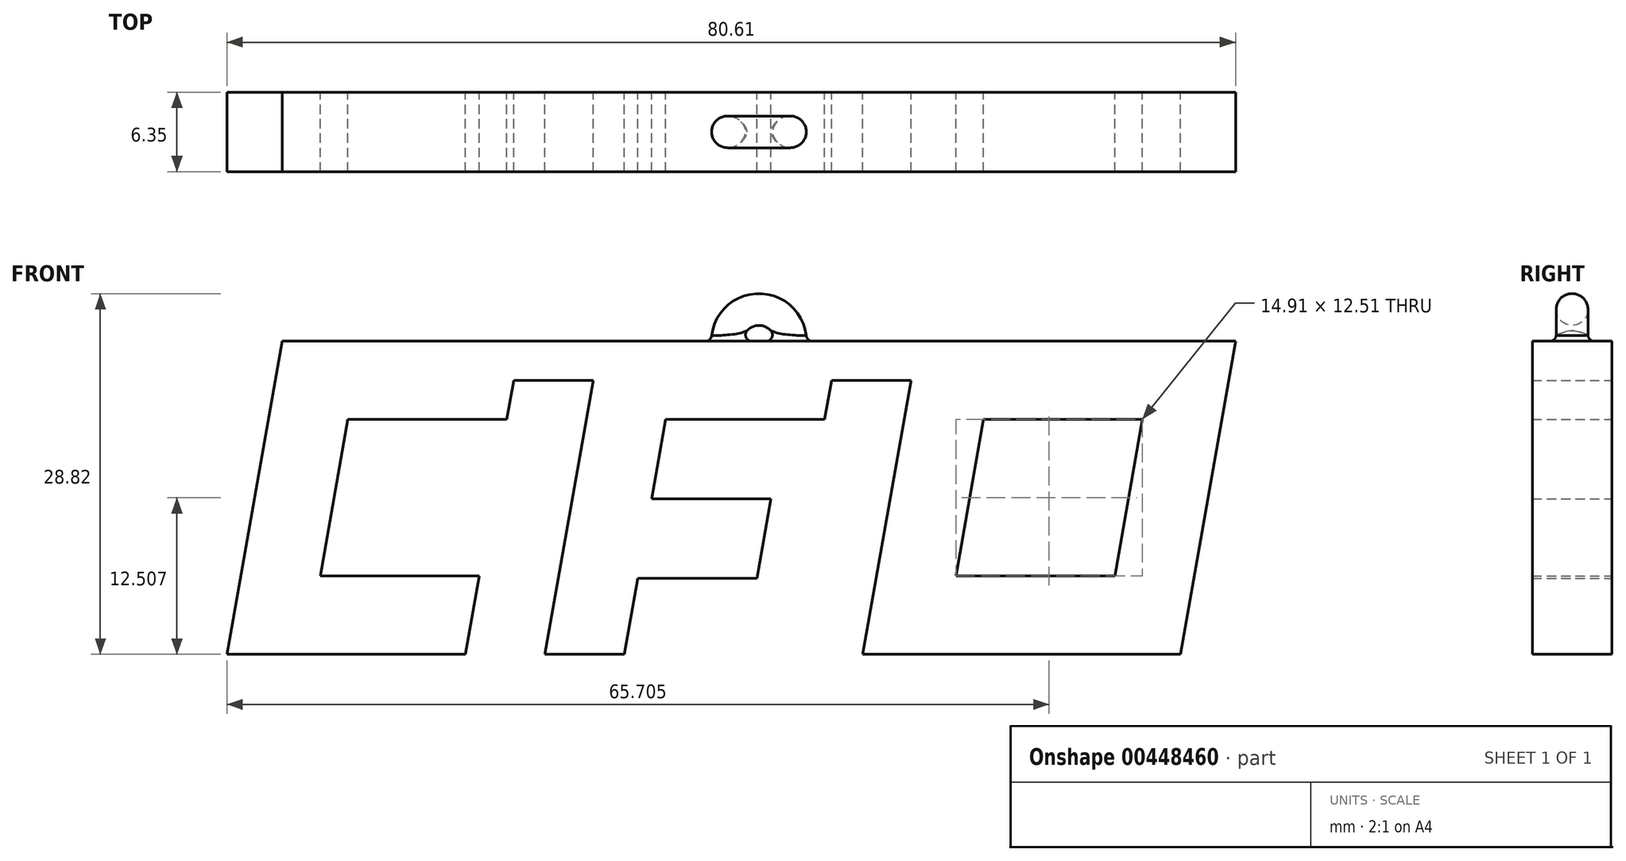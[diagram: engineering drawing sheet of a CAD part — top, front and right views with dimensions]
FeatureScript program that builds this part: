
annotation { "Feature Type Name" : "Feature", "Feature Type Description" : "" }
export const myFeature = defineFeature(function(context is Context, id is Id, definition is map)
    precondition{}
    {
        {
            var Q0;
            Q0=qCreatedBy(makeId("Front.planeOp"),FACE);
            var sketch = newSketch(context, id + "F0", { "sketchPlane" : qUnion([Q0])});
            skLineSegment(sketch, "E0", {"start": v(0, 0) * mm, "end": v(4.41, 25.01) * mm});
            skLineSegment(sketch, "E1", {"start": v(0, 0) * mm, "end": v(25.4, 0) * mm});
            skLineSegment(sketch, "E2", {"start": v(4.41, 25.01) * mm, "end": v(29.81, 25.01) * mm});
            skLineSegment(sketch, "E3", {"start": v(0, 0) * mm, "end": v(0, 25.4) * mm});
            skLineSegment(sketch, "E4", {"start": v(29.81, 25.01) * mm, "end": v(28.7, 18.76) * mm});
            skLineSegment(sketch, "E5", {"start": v(25.4, 0) * mm, "end": v(26.5, 6.25) * mm});
            skLineSegment(sketch, "E6", {"start": v(26.5, 6.25) * mm, "end": v(7.45, 6.25) * mm});
            skLineSegment(sketch, "E7", {"start": v(28.7, 18.76) * mm, "end": v(9.66, 18.76) * mm});
            skLineSegment(sketch, "E8", {"start": v(9.66, 18.76) * mm, "end": v(7.45, 6.25) * mm});
            skLineSegment(sketch, "E9", {"start": v(25.4, 0) * mm, "end": v(29.81, 25.01) * mm});
            skLineSegment(sketch, "E10", {"start": v(29.81, 25.01) * mm, "end": v(55.21, 25.01) * mm});
            skLineSegment(sketch, "E11", {"start": v(55.21, 25.01) * mm, "end": v(54.1, 18.76) * mm});
            skLineSegment(sketch, "E12", {"start": v(25.4, 0) * mm, "end": v(31.75, 0) * mm});
            skLineSegment(sketch, "E13", {"start": v(31.75, 0) * mm, "end": v(36.16, 25.01) * mm});
            skLineSegment(sketch, "E14", {"start": v(54.1, 18.76) * mm, "end": v(35.06, 18.76) * mm});
            skLineSegment(sketch, "E15", {"start": v(33.94, 12.41) * mm, "end": v(52.99, 12.41) * mm});
            skLineSegment(sketch, "E16", {"start": v(54.1, 18.76) * mm, "end": v(48.73, -11.73) * mm});
            skLineSegment(sketch, "E17", {"start": v(32.82, 6.06) * mm, "end": v(51.87, 6.06) * mm});
            skLineSegment(sketch, "E18", {"start": v(43.46, 12.41) * mm, "end": v(42.34, 6.06) * mm});
            skLineSegment(sketch, "E19", {"start": v(50.8, 0) * mm, "end": v(76.2, 0) * mm});
            skLineSegment(sketch, "E20", {"start": v(76.2, 0) * mm, "end": v(80.61, 25.01) * mm});
            skLineSegment(sketch, "E21", {"start": v(80.61, 25.01) * mm, "end": v(74.26, 25.01) * mm});
            skLineSegment(sketch, "E22", {"start": v(74.26, 25.01) * mm, "end": v(69.85, 0) * mm});
            skLineSegment(sketch, "E23", {"start": v(55.21, 25.01) * mm, "end": v(61.56, 25.01) * mm});
            skLineSegment(sketch, "E24", {"start": v(61.56, 25.01) * mm, "end": v(57.15, 0) * mm});
            skLineSegment(sketch, "E25", {"start": v(61.56, 25.01) * mm, "end": v(74.26, 25.01) * mm});
            skLineSegment(sketch, "E26", {"start": v(67.91, 25.01) * mm, "end": v(66.8, 18.76) * mm});
            skLineSegment(sketch, "E27", {"start": v(66.8, 18.76) * mm, "end": v(60.46, 18.76) * mm});
            skLineSegment(sketch, "E28", {"start": v(60.46, 18.76) * mm, "end": v(73.16, 18.76) * mm});
            skLineSegment(sketch, "E29", {"start": v(63.5, 0) * mm, "end": v(64.6, 6.25) * mm});
            skLineSegment(sketch, "E30", {"start": v(64.6, 6.25) * mm, "end": v(58.25, 6.25) * mm});
            skLineSegment(sketch, "E31", {"start": v(58.25, 6.25) * mm, "end": v(70.95, 6.25) * mm});
            skLineSegment(sketch, "E32", {"start": v(23.46, 25.01) * mm, "end": v(22.9, 21.89) * mm});
            skLineSegment(sketch, "E33", {"start": v(22.9, 21.89) * mm, "end": v(29.26, 21.89) * mm});
            skLineSegment(sketch, "E34", {"start": v(22.9, 21.89) * mm, "end": v(19.05, 0) * mm});
            skLineSegment(sketch, "E35", {"start": v(48.86, 25.01) * mm, "end": v(48.3, 21.89) * mm});
            skLineSegment(sketch, "E36", {"start": v(48.3, 21.89) * mm, "end": v(54.66, 21.89) * mm});
            skLineSegment(sketch, "E37", {"start": v(48.3, 21.89) * mm, "end": v(46.73, 12.93) * mm});
            skSolve(sketch);
        }
        {
            var Q0;
            {var subQ1=sQuery(id+"F0.wireOp",EDGE,"E0");Q0=makeQuery(id+"F0.imprint","IMPRINT",FACE,{"disambiguationData":[TD([[makeQuery(id+"F0.imprint","IMPRINT",EDGE,{"derivedFrom":subQ1}),-1.0]])]});}
            var Q1;
            {var subQ10=sQuery(id+"F0.wireOp",EDGE,"E12");Q1=makeQuery(id+"F0.imprint","IMPRINT",FACE,{"disambiguationData":[TD([[makeQuery(id+"F0.imprint","IMPRINT",EDGE,{"derivedFrom":subQ10}),1.0]])]});}
            var Q2;
            {var subQ5=sQuery(id+"F0.wireOp",EDGE,"E18");Q2=makeQuery(id+"F0.imprint","IMPRINT",FACE,{"disambiguationData":[TD([[makeQuery(id+"F0.imprint","IMPRINT",EDGE,{"derivedFrom":subQ5}),-1.0]])]});}
            var Q3;
            {var subQ6=sQuery(id+"F0.wireOp",EDGE,"E23");Q3=makeQuery(id+"F0.imprint","IMPRINT",FACE,{"disambiguationData":[TD([[makeQuery(id+"F0.imprint","IMPRINT",EDGE,{"derivedFrom":subQ6}),-1.0]])]});}
            var Q4;
            {var subQ5=sQuery(id+"F0.wireOp",EDGE,"E26");Q4=makeQuery(id+"F0.imprint","IMPRINT",FACE,{"disambiguationData":[TD([[makeQuery(id+"F0.imprint","IMPRINT",EDGE,{"derivedFrom":subQ5}),-1.0]])]});}
            var Q5;
            {var subQ5=sQuery(id+"F0.wireOp",EDGE,"E26");Q5=makeQuery(id+"F0.imprint","IMPRINT",FACE,{"disambiguationData":[TD([[makeQuery(id+"F0.imprint","IMPRINT",EDGE,{"derivedFrom":subQ5}),1.0]])]});}
            var Q6;
            {var subQ3=sQuery(id+"F0.wireOp",EDGE,"E29");Q6=makeQuery(id+"F0.imprint","IMPRINT",FACE,{"disambiguationData":[TD([[makeQuery(id+"F0.imprint","IMPRINT",EDGE,{"derivedFrom":subQ3}),1.0]])]});}
            var Q7;
            {var subQ3=sQuery(id+"F0.wireOp",EDGE,"E29");Q7=makeQuery(id+"F0.imprint","IMPRINT",FACE,{"disambiguationData":[TD([[makeQuery(id+"F0.imprint","IMPRINT",EDGE,{"derivedFrom":subQ3}),-1.0]])]});}
            var Q8;
            {var subQ3=sQuery(id+"F0.wireOp",EDGE,"E20");Q8=makeQuery(id+"F0.imprint","IMPRINT",FACE,{"disambiguationData":[TD([[makeQuery(id+"F0.imprint","IMPRINT",EDGE,{"derivedFrom":subQ3}),1.0]])]});}
            var Q9;
            {var subQ3=sQuery(id+"F0.wireOp",EDGE,"E32");Q9=makeQuery(id+"F0.imprint","IMPRINT",FACE,{"disambiguationData":[TD([[makeQuery(id+"F0.imprint","IMPRINT",EDGE,{"derivedFrom":subQ3}),1.0]])]});}
            var Q10;
            {var subQ5=sQuery(id+"F0.wireOp",EDGE,"E35");Q10=makeQuery(id+"F0.imprint","IMPRINT",FACE,{"disambiguationData":[TD([[makeQuery(id+"F0.imprint","IMPRINT",EDGE,{"derivedFrom":subQ5}),-1.0]])]});}
            var Q11;
            {var subQ3=sQuery(id+"F0.wireOp",EDGE,"E35");Q11=makeQuery(id+"F0.imprint","IMPRINT",FACE,{"disambiguationData":[TD([[makeQuery(id+"F0.imprint","IMPRINT",EDGE,{"derivedFrom":subQ3}),1.0]])]});}
            extrude(context, id + "F1", {"entities" : qUnion([Q0, Q1, Q2, Q3, Q4, Q5, Q6, Q7, Q8, Q9, Q10, Q11]), "depth" : 6.35 * mm});
        }
        {
            var Q0;
            Q0=makeQuery(id+"F1.opExtrude","SWEPT_FACE",FACE,{"disambiguationData":[OSD([sQuery(id+"F0.wireOp",EDGE,"E2"),sQuery(id+"F0.wireOp",EDGE,"E10"),sQuery(id+"F0.wireOp",EDGE,"E21"),sQuery(id+"F0.wireOp",EDGE,"E23"),sQuery(id+"F0.wireOp",EDGE,"E25")])]});
            var sketch = newSketch(context, id + "F2", { "sketchPlane" : qUnion([Q0])});
            skLineSegment(sketch, "E38", {"start": v(42.51, 0) * mm, "end": v(42.51, -6.35) * mm});
            skLineSegment(sketch, "E39", {"start": v(42.51, -3.18) * mm, "end": v(45.05, -3.18) * mm});
            skCircle(sketch, "E40", {"center": v(45.05, -3.18) * mm, "radius": 1.27 * mm});
            skSolve(sketch);
        }
        {
            var Q0;
            Q0 = qSketchRegion(id + "F2", true);
            var Q1;
            Q1=sQuery(id+"F2.wireOp",EDGE,"E38");
            revolve(context, id + "F3", {"operationType" : NewBodyOperationType.ADD, "entities" : qUnion([Q0]), "axis" : qUnion([Q1]), "revolveType" : RevolveType.FULL});
        }
        {
            var Q0;
            Q0=makeQuery(id+"F3.boolean.opBoolean","INTERSECT",EDGE,{"disambiguationData":[OD(0.0)],"derivedFrom":[makeQuery(id+"F1.opExtrude","SWEPT_FACE",FACE,{"disambiguationData":[OSD([sQuery(id+"F0.wireOp",EDGE,"E2"),sQuery(id+"F0.wireOp",EDGE,"E10"),sQuery(id+"F0.wireOp",EDGE,"E21"),sQuery(id+"F0.wireOp",EDGE,"E23"),sQuery(id+"F0.wireOp",EDGE,"E25")])]}),makeQuery(id+"F3.opRevolve","SWEPT_FACE",FACE,{"disambiguationData":[OSD([sQuery(id+"F2.wireOp",EDGE,"E40")])]})]});
            var Q1;
            Q1=makeQuery(id+"F3.boolean.opBoolean","INTERSECT",EDGE,{"disambiguationData":[OD(1.0)],"derivedFrom":[makeQuery(id+"F1.opExtrude","SWEPT_FACE",FACE,{"disambiguationData":[OSD([sQuery(id+"F0.wireOp",EDGE,"E2"),sQuery(id+"F0.wireOp",EDGE,"E10"),sQuery(id+"F0.wireOp",EDGE,"E21"),sQuery(id+"F0.wireOp",EDGE,"E23"),sQuery(id+"F0.wireOp",EDGE,"E25")])]}),makeQuery(id+"F3.opRevolve","SWEPT_FACE",FACE,{"disambiguationData":[OSD([sQuery(id+"F2.wireOp",EDGE,"E40")])]})]});
            fillet(context, id + "F4", {"entities" : qUnion([Q0, Q1]), "radius" : 0.5 * mm, "tangentPropagation" : true, "allowEdgeOverflow" : false});
        }
    });
